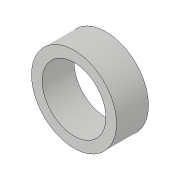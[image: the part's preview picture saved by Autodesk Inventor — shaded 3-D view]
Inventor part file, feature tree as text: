
AUTODESK INVENTOR PART (.ipt)
format: ipt  version: 2018.3 (Build 223284000, 284)  size: 87,040 bytes
history: native  units: in
note: dims shown in document units (in); Inventor stores cm internally (conversion verified against a paired STEP export)
features: extrude x2, sketch x2
ambient origin geometry x8: Origin, YZ Plane, XZ Plane, XY Plane, X Axis, Y Axis, Z Axis, Center Point
bodies: Solid1 (feature_tree)
feature tree (4):
  extrude  "Extrusion1"  Depth=0.094in TaperAngle=0.0deg
  extrude  "Extrusion2"  Depth=0.125in TaperAngle=0.0deg
  sketch  "Sketch1"  dims[d0=0.25in d1=0.094in d2=0.0in]
  sketch  "Sketch2"  dims[d3=0.1875in d4=0.125in d5=0.0in]
